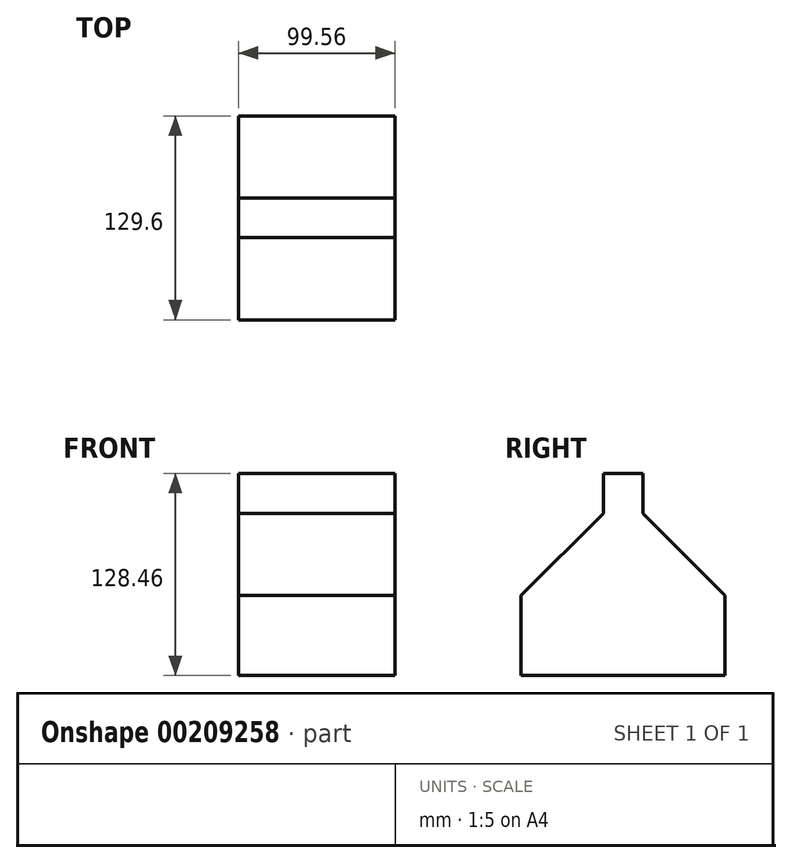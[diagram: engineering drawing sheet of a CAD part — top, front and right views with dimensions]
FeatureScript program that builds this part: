
annotation { "Feature Type Name" : "Feature", "Feature Type Description" : "" }
export const myFeature = defineFeature(function(context is Context, id is Id, definition is map)
    precondition{}
    {
        {
            var Q0;
            Q0=qCreatedBy(makeId("Right.planeOp"),FACE);
            var sketch = newSketch(context, id + "F0", { "sketchPlane" : qUnion([Q0])});
            skLineSegment(sketch, "E0.bottom", {"start": v(64.8, -60.78) * mm, "end": v(-64.8, -60.78) * mm});
            skLineSegment(sketch, "E0.left", {"start": v(64.8, -60.78) * mm, "end": v(64.8, -9.98) * mm});
            skLineSegment(sketch, "E0.right", {"start": v(-64.8, -60.78) * mm, "end": v(-64.8, -9.98) * mm});
            skPoint(sketch, "E0.middle", {"position": v(0, -35.38) * mm});
            skLineSegment(sketch, "E1", {"start": v(64.8, -9.98) * mm, "end": v(12.54, 42.28) * mm});
            skLineSegment(sketch, "E2", {"start": v(12.54, 67.68) * mm, "end": v(12.54, 42.28) * mm});
            skLineSegment(sketch, "E3", {"start": v(12.54, 67.68) * mm, "end": v(0, 67.68) * mm});
            skLineSegment(sketch, "E4.MirrorCS", {"start": v(-12.54, 67.68) * mm, "end": v(0, 67.68) * mm});
            skLineSegment(sketch, "E5.MirrorCS", {"start": v(-12.54, 67.68) * mm, "end": v(-12.54, 42.28) * mm});
            skLineSegment(sketch, "E6.MirrorCS", {"start": v(-64.8, -9.98) * mm, "end": v(-12.54, 42.28) * mm});
            skSolve(sketch);
        }
        {
            var Q0;
            Q0=makeQuery(id+"F0.imprint","IMPRINT",FACE,{"disambiguationData":[TD([[makeQuery(id+"F0.imprint","IMPRINT",EDGE,{"derivedFrom":sQuery(id+"F0.wireOp",EDGE,"E0.bottom")}),-1.0]])]});
            extrude(context, id + "F1", {"entities" : qUnion([Q0]), "endBound" : BoundingType.SYMMETRIC, "oppositeDirection" : true, "depth" : 99.57 * mm});
        }
    });
